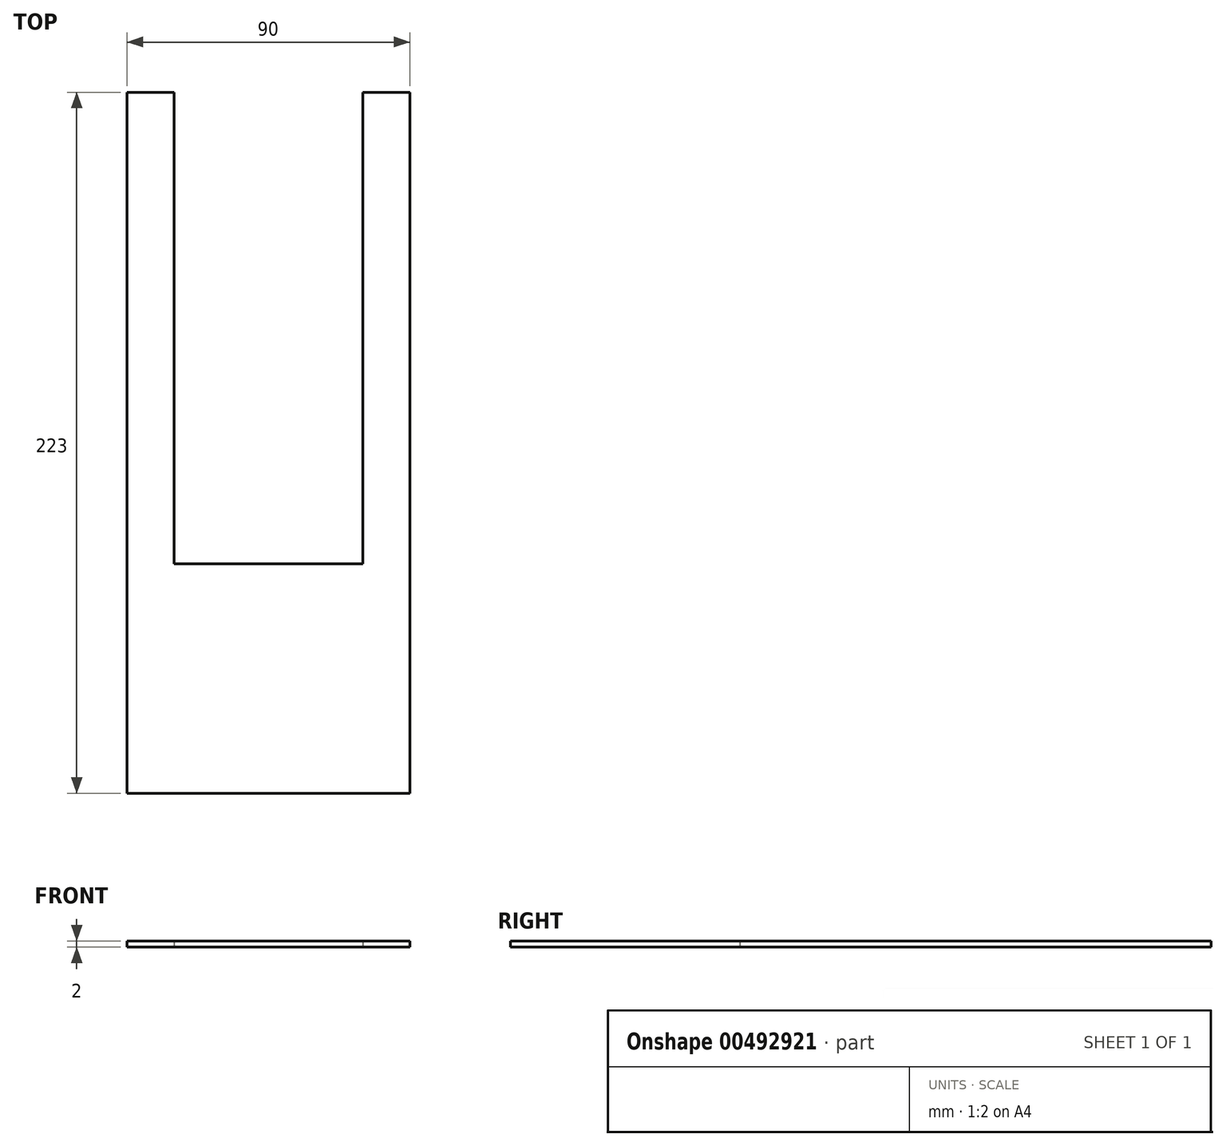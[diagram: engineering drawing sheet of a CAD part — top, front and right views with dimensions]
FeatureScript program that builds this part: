
annotation { "Feature Type Name" : "Feature", "Feature Type Description" : "" }
export const myFeature = defineFeature(function(context is Context, id is Id, definition is map)
    precondition{}
    {
        {
            var Q0;
            Q0=qCreatedBy(makeId("Top.planeOp"),FACE);
            var sketch = newSketch(context, id + "F0", { "sketchPlane" : qUnion([Q0])});
            skLineSegment(sketch, "E0.bottom", {"start": v(45, 111.5) * mm, "end": v(-45, 111.5) * mm});
            skLineSegment(sketch, "E0.top", {"start": v(45, -111.5) * mm, "end": v(-45, -111.5) * mm});
            skLineSegment(sketch, "E0.left", {"start": v(45, 111.5) * mm, "end": v(45, -111.5) * mm});
            skLineSegment(sketch, "E0.right", {"start": v(-45, 111.5) * mm, "end": v(-45, -111.5) * mm});
            skPoint(sketch, "E0.middle", {"position": v(0, 0) * mm});
            skLineSegment(sketch, "E1.bottom", {"start": v(-30, 111.5) * mm, "end": v(30, 111.5) * mm});
            skLineSegment(sketch, "E1.top", {"start": v(-30, -38.5) * mm, "end": v(30, -38.5) * mm});
            skLineSegment(sketch, "E1.left", {"start": v(-30, 111.5) * mm, "end": v(-30, -38.5) * mm});
            skLineSegment(sketch, "E1.right", {"start": v(30, 111.5) * mm, "end": v(30, -38.5) * mm});
            skSolve(sketch);
        }
        {
            var Q0;
            Q0=makeQuery(id+"F0.imprint","IMPRINT",FACE,{"disambiguationData":[TD([[makeQuery(id+"F0.imprint","IMPRINT",EDGE,{"derivedFrom":sQuery(id+"F0.wireOp",EDGE,"E0.top")}),-1.0]])]});
            extrude(context, id + "F1", {"entities" : qUnion([Q0]), "depth" : 2 * mm, "offsetDistance" : 25 * mm});
        }
    });
